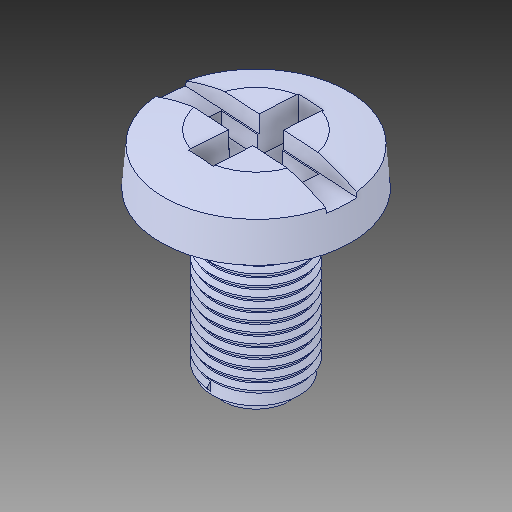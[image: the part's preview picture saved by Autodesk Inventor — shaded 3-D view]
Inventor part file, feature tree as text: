
AUTODESK INVENTOR PART (.ipt)
format: ipt  version: 2018 (Build 220112000, 112)  size: 689,664 bytes
history: native  units: in
note: dims shown in document units (in); Inventor stores cm internally (conversion verified against a paired STEP export)
features: chamfer x1
ambient origin geometry x8: Origin, YZ Plane, XZ Plane, XY Plane, X Axis, Y Axis, Z Axis, Center Point
bodies: Solid1 (feature_tree)
feature tree (1):
  chamfer  "Chamfer1"  [1 undecoded]
note: 1 required parameter value undecoded (feature->parameter linkage not recoverable at this tier; creation-order binding heuristic only, values carry confidence <= 0.55)
